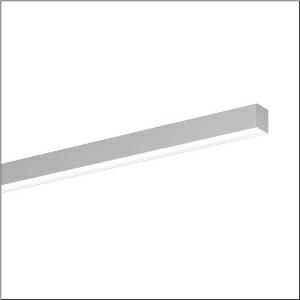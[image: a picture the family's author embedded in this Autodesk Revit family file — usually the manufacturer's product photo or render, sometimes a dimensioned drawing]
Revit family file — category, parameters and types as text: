
# Revit family: silica_r__21_51mx23dl45sb_0964
name_source: partatom
category: Lighting Fixtures
units: mm (PartAtom-declared; Revit-internal decimal feet)

## family parameters
Cut with Voids When Loaded = No
Host = Face
Light Source = No
Part Type = Normal
Room Calculation Point = No
Round Connector Dimension = Use Diameter
Shared = No

## types (1)
- --- (1 x LED, 5740 lm, 38.2 W, 4000K)
    Apparent Load = 38 VA
    CIE Flux Codes = 78 96 99 100 100
    Color Rendering = 80
    Color Temperature = 4000K
    Default Elevation = 1800 mm
    Description = Silica® 21, office luminaire, primary optical cover: prismatic diffuser, of PMMA, CAT 2 (L<= 3000cd/m²), light emission: direct distribution, primary light characteristic: symmetric, installation type: surface-mounted, LED, rated luminous flux: 5.740lm, luminous efficacy: 150lm/W, light colour: 840, colour temperature: 4000K, control gear: DALI 2, with terminal, 3+2-pole, max. 2.5mm², mains connection: 220..240V, AC, 50/60Hz, rated input power: 38.2W, luminaire housing, of aluminium, metallic grey (RAL 9006), length: 2.100mm, width: 53mm, height: 53mm, protection rating (complete): IP20, insulation class (complete): insulation class I (protective earthing), certification: CE, permissible operating ambient temperature: 0..+35°C, standard: EN 50419, packaging unit: 1 piece
    Height = 53 mm
    Lamp = 1 x LED
    Lamp Light Flux = 5740 lm
    Lamp Power = 38.2 W
    Lamp count = 1
    Length = 2104 mm
    Luminous efficacy = 150 lm/W
    Manufacturer = Siteco
    ModVariant = No
    Model = 51MX23DL45SB
    Mounting Place = Ceiling
    Mounting Type = Surface mounted
    Number of Poles = 1
    OnlyDefault = Yes
    Power Factor = 1
    Product Name = Silica® 21
    Product group = office luminaire | ceiling mounted
    ProductGroupID = 303
    Protection Class = Protection class I
    Protection Degree = IP 20
    RLX_Detail_Level = 1
    RLX_Emergency_Light_Flux = 0 lm
    RLX_Emergency_Type = 0
    RLX_Emergency_Type_DB = No
    RlxData = <blob elided: 17961 chars, md5=8ec47142>
    Socket = socket
    Standby Power = 0 W
    System Light Flux = 5740 lm
    System Power = 38 W
    Type Comments = factory setting: luminous flux: 100 % | dim-lin: 254 | 302 mA
    Type Image = l_1335933.jpg
    URL = http://relux.com
    VarID = @adj_084841
    Voltage = 0 V
    Weight = 0.00 kg
    Width = 53 mm

## geometry (parser evidence)
native form markers: Blend x4, Sweep x11
no freeform markers — native parametric forms only
